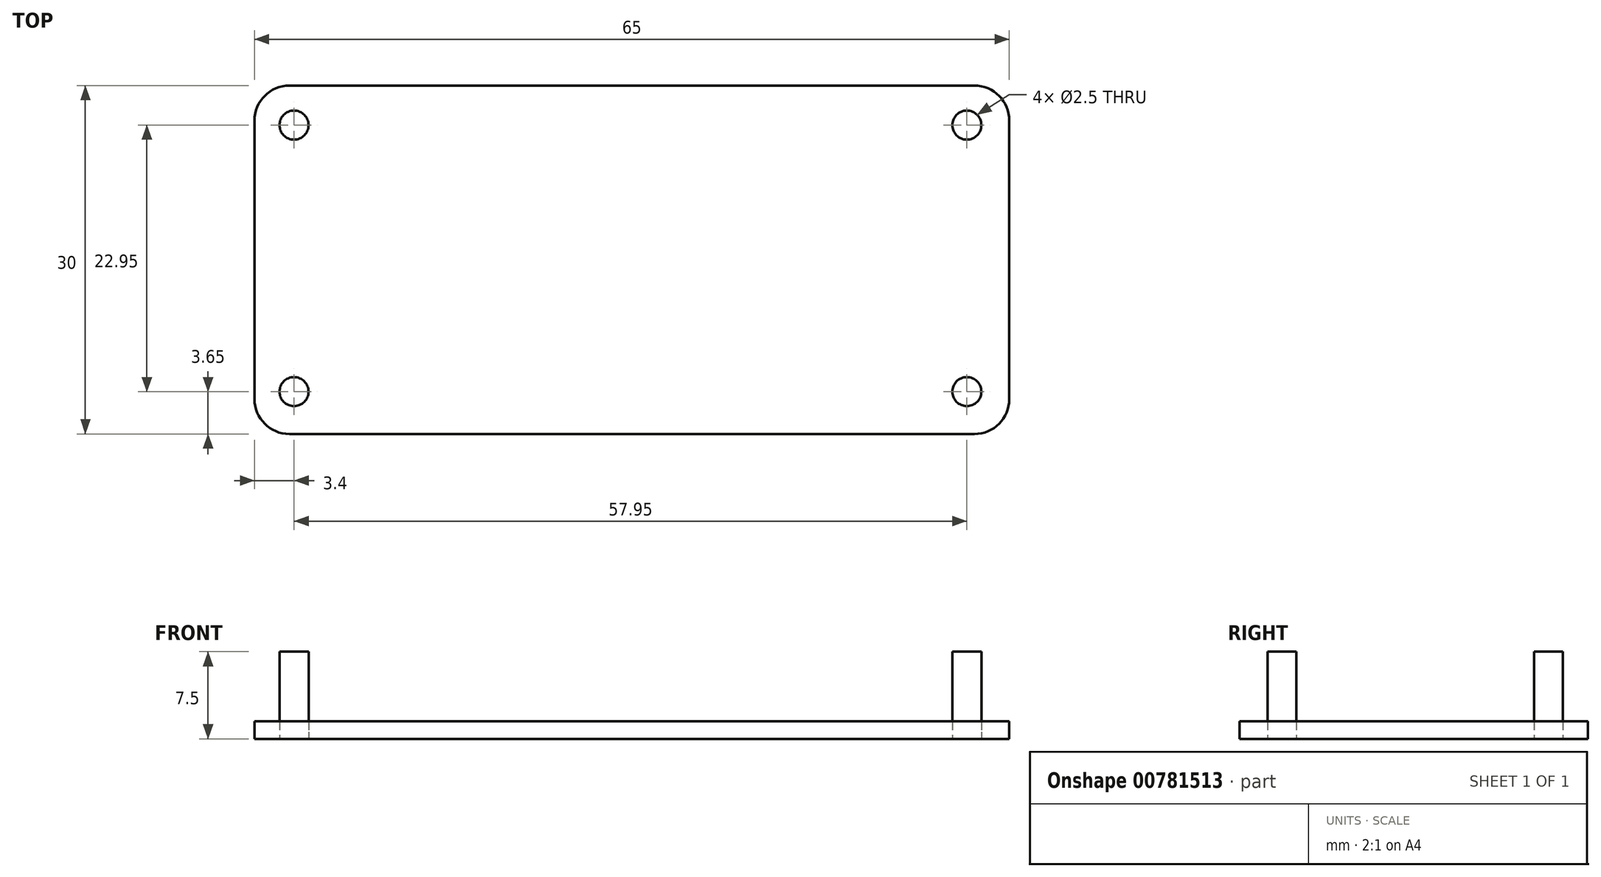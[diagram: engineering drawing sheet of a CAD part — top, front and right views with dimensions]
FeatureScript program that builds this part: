
annotation { "Feature Type Name" : "Feature", "Feature Type Description" : "" }
export const myFeature = defineFeature(function(context is Context, id is Id, definition is map)
    precondition{}
    {
        {
            var Q0;
            Q0=qCreatedBy(makeId("Top.planeOp"),FACE);
            var sketch = newSketch(context, id + "F0", { "sketchPlane" : qUnion([Q0])});
            skLineSegment(sketch, "E0.bottom", {"start": v(29.5, -15) * mm, "end": v(-29.5, -15) * mm});
            skLineSegment(sketch, "E0.top", {"start": v(29.5, 15) * mm, "end": v(-29.5, 15) * mm});
            skLineSegment(sketch, "E0.left", {"start": v(32.5, -12) * mm, "end": v(32.5, 12) * mm});
            skLineSegment(sketch, "E0.right", {"start": v(-32.5, -12) * mm, "end": v(-32.5, 12) * mm});
            skPoint(sketch, "E0.middle", {"position": v(0, 0) * mm});
            skCircle(sketch, "E1", {"center": v(-29.1, 11.6) * mm, "radius": 1.25 * mm});
            skCircle(sketch, "E2", {"center": v(28.85, 11.6) * mm, "radius": 1.25 * mm});
            skCircle(sketch, "E3", {"center": v(-29.1, -11.35) * mm, "radius": 1.25 * mm});
            skCircle(sketch, "E4", {"center": v(28.85, -11.35) * mm, "radius": 1.25 * mm});
            skPoint(sketch, "E5.visualSharp", {"position": v(-32.5, 15) * mm});
            skArc(sketch, "E5.filletArc", {"start": v(-29.5, 15) * mm, "mid": v(-31.62, 14.12) * mm, "end": v(-32.5, 12) * mm});
            skPoint(sketch, "E6.visualSharp", {"position": v(32.5, 15) * mm});
            skArc(sketch, "E6.filletArc", {"start": v(32.5, 12) * mm, "mid": v(31.62, 14.12) * mm, "end": v(29.5, 15) * mm});
            skPoint(sketch, "E7.visualSharp", {"position": v(32.5, -15) * mm});
            skArc(sketch, "E7.filletArc", {"start": v(29.5, -15) * mm, "mid": v(31.62, -14.12) * mm, "end": v(32.5, -12) * mm});
            skPoint(sketch, "E8.visualSharp", {"position": v(-32.5, -15) * mm});
            skArc(sketch, "E8.filletArc", {"start": v(-32.5, -12) * mm, "mid": v(-31.62, -14.12) * mm, "end": v(-29.5, -15) * mm});
            skSolve(sketch);
        }
        {
            var Q0;
            Q0=makeQuery(id+"F0.imprint","IMPRINT",FACE,{"disambiguationData":[TD([[makeQuery(id+"F0.imprint","IMPRINT",EDGE,{"derivedFrom":sQuery(id+"F0.wireOp",EDGE,"E3")}),1.0]])]});
            var Q1;
            Q1=makeQuery(id+"F0.imprint","IMPRINT",FACE,{"disambiguationData":[TD([[makeQuery(id+"F0.imprint","IMPRINT",EDGE,{"derivedFrom":sQuery(id+"F0.wireOp",EDGE,"E1")}),1.0]])]});
            var Q2;
            Q2=makeQuery(id+"F0.imprint","IMPRINT",FACE,{"disambiguationData":[TD([[makeQuery(id+"F0.imprint","IMPRINT",EDGE,{"derivedFrom":sQuery(id+"F0.wireOp",EDGE,"E2")}),1.0]])]});
            var Q3;
            Q3=makeQuery(id+"F0.imprint","IMPRINT",FACE,{"disambiguationData":[TD([[makeQuery(id+"F0.imprint","IMPRINT",EDGE,{"derivedFrom":sQuery(id+"F0.wireOp",EDGE,"E4")}),1.0]])]});
            var Q4;
            Q4=sQuery(id+"F0.wireOp",EDGE,"E1");
            var Q5;
            Q5=sQuery(id+"F0.wireOp",EDGE,"E3");
            var Q6;
            Q6=sQuery(id+"F0.wireOp",EDGE,"E2");
            var Q7;
            Q7=sQuery(id+"F0.wireOp",EDGE,"E4");
            extrude(context, id + "F1", {"entities" : qUnion([Q0, Q1, Q2, Q3]), "surfaceEntities" : qUnion([Q4, Q5, Q6, Q7]), "depth" : 7.5 * mm, "offsetDistance" : 25 * mm});
        }
        {
            var Q0;
            Q0=qSketchRegion(id+"F0",true);
            extrude(context, id + "F2", {"entities" : qUnion([Q0]), "depth" : 1.5 * mm, "offsetDistance" : 25 * mm});
        }
    });
